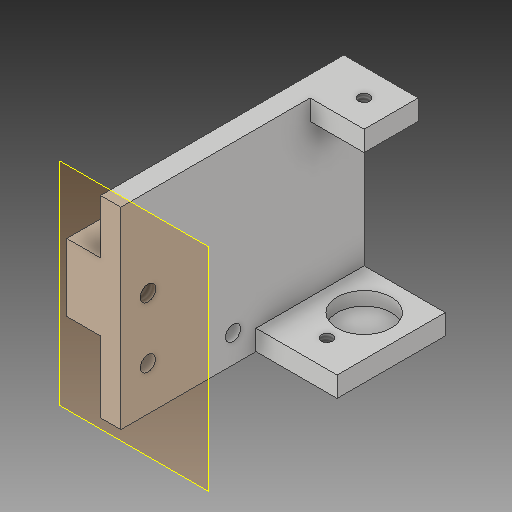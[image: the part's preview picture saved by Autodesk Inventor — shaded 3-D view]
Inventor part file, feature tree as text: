
AUTODESK INVENTOR PART (.ipt)
format: ipt  version: 2019 (Build 230136000, 136)  size: 205,312 bytes
history: native  units: in
note: dims shown in document units (in); Inventor stores cm internally (conversion verified against a paired STEP export)
features: projected_geometry x9, sketch x8, hole x5, extrude x4, plane x1, mirror x1
ambient origin geometry x8: Origin, YZ Plane, XZ Plane, XY Plane, X Axis, Y Axis, Z Axis, Center Point
bodies: Solid1 (feature_tree)
feature tree (28):
  extrude  "Extrusion1"  Depth=2.25in
  extrude  "Extrusion2"  Depth=0.5in
  extrude  "Extrusion3"  Depth=0.5in TaperAngle=0.0deg
  extrude  "Extrusion4"  Depth=0.75in TaperAngle=0.0deg
  hole  "Hole1"  [1 undecoded]
  hole  "Hole2"  [1 undecoded]
  hole  "Hole3"  [1 undecoded]
  hole  "Hole4"  [1 undecoded]
  plane  "Work Plane1"
  mirror  "Mirror1"
  hole  "Hole5"  [1 undecoded]
  sketch  "Sketch1"  dims[d0=1.7812in d1=2.25in]
  sketch  "Sketch2"  dims[d2=0.1875in d3=0.0in d4=0.5in]
  projected_geometry  "Projected Loop1"
  sketch  "Sketch3"  dims[d5=0.1875in d6=0.5in d7=0.0in]
  projected_geometry  "Projected Loop2"
  projected_geometry  "Projected Loop3"
  sketch  "Sketch5"  dims[d8=0.1875in d9=0.75in d10=0.0in]
  projected_geometry  "Projected Loop4"
  projected_geometry  "Projected Loop5"
  sketch  "Sketch6"  dims[d13=0.3125in d14=0.0in d15=0.1875in]
  projected_geometry  "Projected Loop6"
  sketch  "Sketch10"  dims[d16=0.8125in d17=0.25in]
  projected_geometry  "Projected Loop10"
  sketch  "Sketch11"  dims[d18=0.145in d19=0.38in d20=0.375in d21=0.25in d22=0.5635in d23=0.588in d24=0.8108in d25=0.375in]
  projected_geometry  "Projected Loop11"
  sketch  "Sketch12"  dims[d26=0.375in d27=0.5in d28=0.75in d29=0.375in d30=0.25in d31=0.5635in d32=0.125in d33=0.0in d48=0.625in d49=0.5in d50=0.5in d51=0.104in d52=0.276in d53=0.375in d54=0.25in d55=0.5635in d56=0.432in d57=0.8108in d58=0.25in d59=0.104in d60=0.276in d61=0.375in d62=0.25in d63=0.5635in d64=0.432in d65=0.8108in d66=0.406in d67=0.25in d68=0.256in d69=1.0375in d70=0.14in d71=0.75in d72=0.375in d73=0.25in d74=0.5635in d75=1.0in d76=0.8108in]
  projected_geometry  "Projected Loop12"
note: 5 required parameter values undecoded (feature->parameter linkage not recoverable at this tier; creation-order binding heuristic only, values carry confidence <= 0.55)
